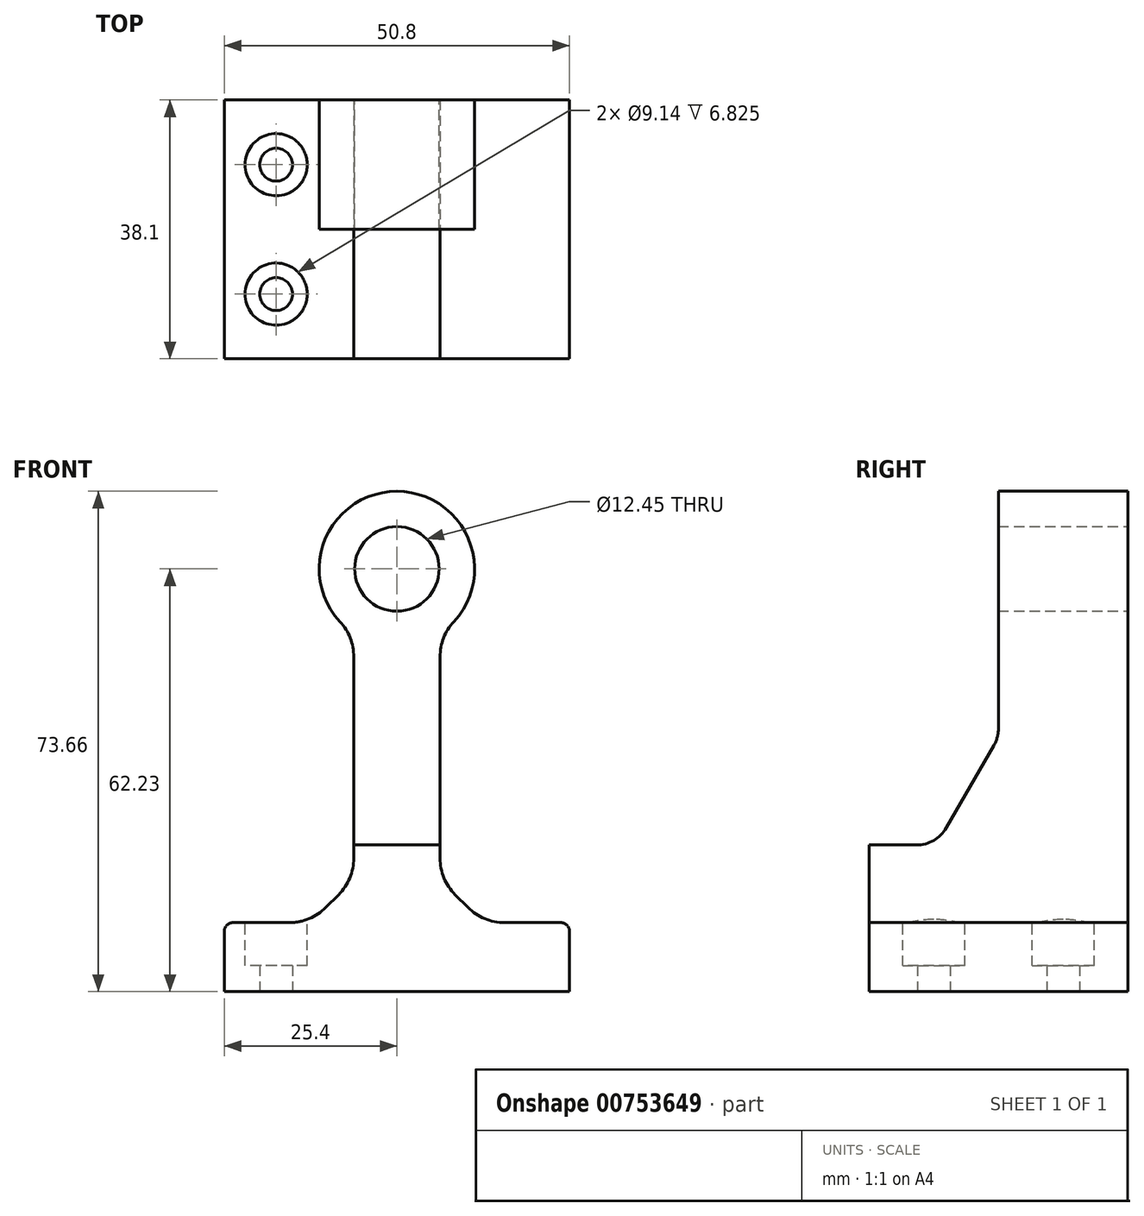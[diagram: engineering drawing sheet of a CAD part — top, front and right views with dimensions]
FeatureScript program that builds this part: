
annotation { "Feature Type Name" : "Feature", "Feature Type Description" : "" }
export const myFeature = defineFeature(function(context is Context, id is Id, definition is map)
    precondition{}
    {
        {
            var Q0;
            Q0=qCreatedBy(makeId("Front.planeOp"),FACE);
            var sketch = newSketch(context, id + "F0", { "sketchPlane" : qUnion([Q0])});
            skLineSegment(sketch, "E0", {"start": v(-25.4, 0) * mm, "end": v(25.4, 0) * mm});
            skLineSegment(sketch, "E1", {"start": v(6.35, 10.16) * mm, "end": v(6.35, 52.73) * mm});
            skLineSegment(sketch, "E2", {"start": v(-6.35, 52.73) * mm, "end": v(-6.35, 10.16) * mm});
            skLineSegment(sketch, "E3", {"start": v(-6.35, 10.16) * mm, "end": v(-25.4, 10.16) * mm});
            skLineSegment(sketch, "E4", {"start": v(-25.4, 10.16) * mm, "end": v(-25.4, 0) * mm});
            skCircle(sketch, "E5", {"center": v(0, 62.23) * mm, "radius": 6.22 * mm});
            skArc(sketch, "E6", {"start": v(6.35, 52.73) * mm, "mid": v(0, 73.66) * mm, "end": v(-6.35, 52.73) * mm});
            skLineSegment(sketch, "E7", {"start": v(6.35, 10.16) * mm, "end": v(25.4, 10.16) * mm});
            skLineSegment(sketch, "E8", {"start": v(25.4, 10.16) * mm, "end": v(25.4, 0) * mm});
            skSolve(sketch);
        }
        {
            var Q0;
            Q0 = qSketchRegion(id + "F0", true);
            extrude(context, id + "F1", {"entities" : qUnion([Q0]), "endBound" : BoundingType.SYMMETRIC, "depth" : 38.1 * mm, "offsetDistance" : 25.4 * mm});
        }
        {
            var Q0;
            Q0=makeQuery(id+"F1.opExtrude","SWEPT_EDGE",EDGE,{"disambiguationData":[OSD([sQuery(id+"F0.wireOp",EDGE,"E2"),sQuery(id+"F0.wireOp",EDGE,"E3")])]});
            var Q1;
            Q1=makeQuery(id+"F1.opExtrude","SWEPT_EDGE",EDGE,{"disambiguationData":[OSD([sQuery(id+"F0.wireOp",EDGE,"E1"),sQuery(id+"F0.wireOp",EDGE,"E7")])]});
            chamfer(context, id + "F2", {"entities" : qUnion([Q0, Q1]), "width" : 6.35 * mm, "tangentPropagation" : true});
        }
        {
            var Q0;
            Q0=makeQuery(id+"F1.opExtrude","SWEPT_FACE",FACE,{"disambiguationData":[OSD([sQuery(id+"F0.wireOp",EDGE,"E0")])]});
            var sketch = newSketch(context, id + "F3", { "sketchPlane" : qUnion([Q0])});
            skCircle(sketch, "E9", {"center": v(-17.78, 9.53) * mm, "radius": 2.41 * mm});
            skCircle(sketch, "E10", {"center": v(-17.78, -9.53) * mm, "radius": 2.41 * mm});
            skSolve(sketch);
        }
        {
            var Q0;
            Q0=makeQuery(id+"F1.opExtrude","SWEPT_EDGE",EDGE,{"disambiguationData":[OSD([sQuery(id+"F0.wireOp",EDGE,"E2"),sQuery(id+"F0.wireOp",EDGE,"E6")])]});
            var Q1;
            {var subQ0=sQuery(id+"F0.wireOp",EDGE,"E2");Q1=makeQuery(id+"F2.opChamfer","BLEND_EDGE",EDGE,{"blendedFrom":[makeQuery(id+"F1.opExtrude","SWEPT_EDGE",EDGE,{"disambiguationData":[OSD([subQ0,sQuery(id+"F0.wireOp",EDGE,"E3")])]}),makeQuery(id+"F1.opExtrude","SWEPT_FACE",FACE,{"disambiguationData":[OSD([subQ0])]})],"blendedInto":[makeQuery(id+"F1.opExtrude","SWEPT_FACE",FACE,{"disambiguationData":[OSD([subQ0])]})]});}
            var Q2;
            {var subQ0=sQuery(id+"F0.wireOp",EDGE,"E3");Q2=makeQuery(id+"F2.opChamfer","BLEND_EDGE",EDGE,{"blendedFrom":[makeQuery(id+"F1.opExtrude","SWEPT_EDGE",EDGE,{"disambiguationData":[OSD([sQuery(id+"F0.wireOp",EDGE,"E2"),subQ0])]}),makeQuery(id+"F1.opExtrude","SWEPT_FACE",FACE,{"disambiguationData":[OSD([subQ0])]})],"blendedInto":[makeQuery(id+"F1.opExtrude","SWEPT_FACE",FACE,{"disambiguationData":[OSD([subQ0])]})]});}
            var Q3;
            {var subQ0=sQuery(id+"F0.wireOp",EDGE,"E7");Q3=makeQuery(id+"F2.opChamfer","BLEND_EDGE",EDGE,{"blendedFrom":[makeQuery(id+"F1.opExtrude","SWEPT_EDGE",EDGE,{"disambiguationData":[OSD([sQuery(id+"F0.wireOp",EDGE,"E1"),subQ0])]}),makeQuery(id+"F1.opExtrude","SWEPT_FACE",FACE,{"disambiguationData":[OSD([subQ0])]})],"blendedInto":[makeQuery(id+"F1.opExtrude","SWEPT_FACE",FACE,{"disambiguationData":[OSD([subQ0])]})]});}
            var Q4;
            {var subQ0=sQuery(id+"F0.wireOp",EDGE,"E1");Q4=makeQuery(id+"F2.opChamfer","BLEND_EDGE",EDGE,{"blendedFrom":[makeQuery(id+"F1.opExtrude","SWEPT_EDGE",EDGE,{"disambiguationData":[OSD([subQ0,sQuery(id+"F0.wireOp",EDGE,"E7")])]}),makeQuery(id+"F1.opExtrude","SWEPT_FACE",FACE,{"disambiguationData":[OSD([subQ0])]})],"blendedInto":[makeQuery(id+"F1.opExtrude","SWEPT_FACE",FACE,{"disambiguationData":[OSD([subQ0])]})]});}
            var Q5;
            Q5=makeQuery(id+"F1.opExtrude","SWEPT_EDGE",EDGE,{"disambiguationData":[OSD([sQuery(id+"F0.wireOp",EDGE,"E1"),sQuery(id+"F0.wireOp",EDGE,"E6")])]});
            fillet(context, id + "F4", {"entities" : qUnion([Q0, Q1, Q2, Q3, Q4, Q5]), "tangentPropagation" : true, "radius" : 7.62 * mm, "defaultsChanged" : true, "vertexSettings" : [], "allowEdgeOverflow" : false});
        }
        {
            var Q0;
            Q0 = qSketchRegion(id + "F3", true);
            extrude(context, id + "F5", {"entities" : qUnion([Q0]), "operationType" : NewBodyOperationType.REMOVE, "endBound" : BoundingType.THROUGH_ALL, "oppositeDirection" : true, "depth" : 25.4 * mm, "offsetDistance" : 25.4 * mm});
        }
        {
            var Q0;
            Q0=makeQuery(id+"F1.opExtrude","SWEPT_FACE",FACE,{"disambiguationData":[OSD([sQuery(id+"F0.wireOp",EDGE,"E3")])]});
            var sketch = newSketch(context, id + "F6", { "sketchPlane" : qUnion([Q0])});
            skCircle(sketch, "E11", {"center": v(-17.78, 9.53) * mm, "radius": 4.57 * mm});
            skCircle(sketch, "E12", {"center": v(-17.78, -9.53) * mm, "radius": 4.57 * mm});
            skSolve(sketch);
        }
        {
            var Q0;
            Q0 = qSketchRegion(id + "F6", true);
            extrude(context, id + "F7", {"entities" : qUnion([Q0]), "operationType" : NewBodyOperationType.REMOVE, "oppositeDirection" : true, "depth" : 6.35 * mm, "offsetDistance" : 25.4 * mm, "hasSecondDirection" : true, "secondDirectionBound" : SecondDirectionBoundingType.THROUGH_ALL, "secondDirectionOppositeDirection" : false, "secondDirectionDepth" : 25.4 * mm});
        }
        {
            var Q0;
            Q0=makeQuery(id+"F1.opExtrude","SWEPT_EDGE",EDGE,{"disambiguationData":[OSD([sQuery(id+"F0.wireOp",EDGE,"E3"),sQuery(id+"F0.wireOp",EDGE,"E4")])]});
            var Q1;
            Q1=makeQuery(id+"F1.opExtrude","SWEPT_EDGE",EDGE,{"disambiguationData":[OSD([sQuery(id+"F0.wireOp",EDGE,"E7"),sQuery(id+"F0.wireOp",EDGE,"E8")])]});
            fillet(context, id + "F8", {"entities" : qUnion([Q0, Q1]), "tangentPropagation" : true, "radius" : 1.27 * mm, "defaultsChanged" : true, "vertexSettings" : [], "allowEdgeOverflow" : false});
        }
        {
            var Q0;
            Q0=qCreatedBy(makeId("Right.planeOp"),FACE);
            var sketch = newSketch(context, id + "F9", { "sketchPlane" : qUnion([Q0])});
            skLineSegment(sketch, "E13", {"start": v(0, 76.9) * mm, "end": v(0, 37.41) * mm});
            skLineSegment(sketch, "E14", {"start": v(0, 37.41) * mm, "end": v(-9.14, 21.6) * mm});
            skLineSegment(sketch, "E15", {"start": v(-9.14, 21.59) * mm, "end": v(-23.65, 21.59) * mm});
            skLineSegment(sketch, "E16", {"start": v(-23.65, 21.59) * mm, "end": v(-23.65, 76.9) * mm});
            skLineSegment(sketch, "E17", {"start": v(-23.65, 76.9) * mm, "end": v(0, 76.9) * mm});
            skSolve(sketch);
        }
        {
            var Q0;
            Q0 = qSketchRegion(id + "F9", true);
            extrude(context, id + "F10", {"entities" : qUnion([Q0]), "operationType" : NewBodyOperationType.REMOVE, "endBound" : BoundingType.SYMMETRIC, "oppositeDirection" : true, "depth" : 50.8 * mm, "offsetDistance" : 25.4 * mm});
        }
        {
            var Q0;
            Q0=makeQuery(id+"F10.boolean.opBoolean","COPY",EDGE,{"derivedFrom":makeQuery(id+"F10.opExtrude","SWEPT_EDGE",EDGE,{"disambiguationData":[OSD([sQuery(id+"F9.wireOp",EDGE,"E13"),sQuery(id+"F9.wireOp",EDGE,"E14")])]})});
            var Q1;
            Q1=makeQuery(id+"F10.boolean.opBoolean","COPY",EDGE,{"derivedFrom":makeQuery(id+"F10.opExtrude","SWEPT_EDGE",EDGE,{"disambiguationData":[OSD([sQuery(id+"F9.wireOp",EDGE,"E14"),sQuery(id+"F9.wireOp",EDGE,"E15")])]})});
            fillet(context, id + "F11", {"entities" : qUnion([Q0, Q1]), "tangentPropagation" : true, "radius" : 5.08 * mm, "defaultsChanged" : false, "vertexSettings" : [], "allowEdgeOverflow" : false});
        }
    });
